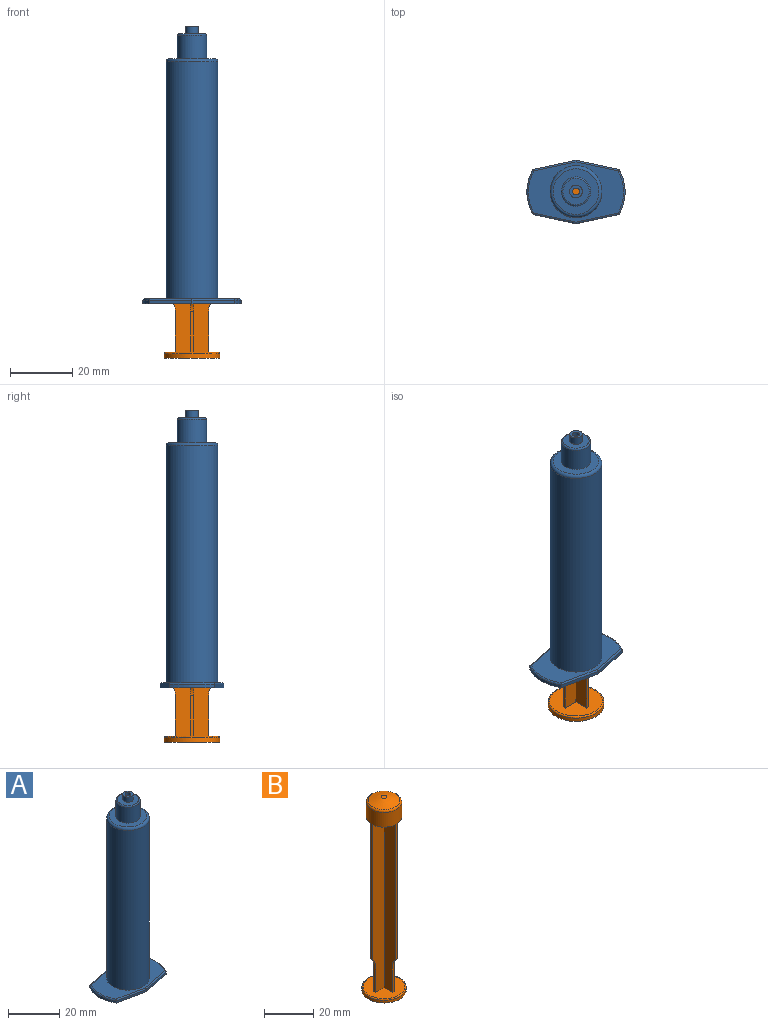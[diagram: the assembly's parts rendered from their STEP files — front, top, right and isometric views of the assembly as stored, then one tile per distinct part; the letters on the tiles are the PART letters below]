
ASSEMBLY  parts=2 mates=1
PART A: 25 faces, bbox 33.8x20.3x89 mm
  f0: cylinder r=7.15mm len=77mm, axis (0,0,-1), area 3459.2mm2, adj f8,f12
  f1: cylinder r=14.22mm len=14.5mm, axis (0,0,-1), area 15.2mm2, adj f2,f6,f8,f19
  f2: plane 13.78x2.9mm, normal (-0.21,-0.98,0), area 14.1mm2, adj f1,f3,f8,f17
  f3: plane 13.78x2.9mm, normal (0.21,-0.98,0), area 14.1mm2, adj f2,f4,f8,f16
  f4: cylinder r=14.22mm len=14.5mm, axis (0,0,-1), area 15.2mm2, adj f3,f5,f8,f18
  f5: plane 13.75x2.9mm, normal (0.21,0.98,0), area 14.1mm2, adj f4,f6,f8,f20
  f6: plane 13.75x2.9mm, normal (-0.21,0.98,0), area 14.1mm2, adj f1,f5,f8,f21
  f7: plane 30.5x19.28mm, normal (0,0,1), area 259mm2, adj f9,f16,f17,f18,f19,f20,f21
  f8: plane 31.5x20.3mm, normal (0,0,-1), area 357.3mm2, adj f0,f1,f2,f3,f4,f5,f6
  f9: cylinder r=8.3mm len=76mm, axis (0,0,-1), area 3963.4mm2, adj f7,f15
  f10: plane 14.6x14.6mm, normal (0,0,1), area 98mm2, adj f13,f15
  f11: cylinder r=1.1mm len=12mm, axis (0,0,-1), area 82.9mm2, adj f12,f22
  f12: plane 14.3x14.3mm, normal (0,0,-1), area 156.8mm2, adj f0,f11
  f13: cylinder r=4.7mm len=9.4mm, axis (0,0,-1), area 221.5mm2, adj f10,f24
  f14: plane 8.4x8.4mm, normal (0,0,1), area 42.2mm2, adj f23,f24
  f15: torus R=7.3mm, axis (0,0,1), area 78.3mm2, adj f9,f10
  f16: cylinder r=0.5mm len=13.88mm, axis (-0.98,-0.21,0), area 11mm2, adj f3,f7,f17,f18
  f17: cylinder r=0.5mm len=13.88mm, axis (-0.98,0.21,0), area 11mm2, adj f2,f7,f16,f19
  f18: torus R=13.72mm, axis (0,0,1), area 11.7mm2, adj f4,f7,f16,f20
  f19: torus R=13.72mm, axis (0,0,1), area 11.7mm2, adj f1,f7,f17,f21
  f20: cylinder r=0.5mm len=13.85mm, axis (0.98,-0.21,0), area 10.9mm2, adj f5,f7,f18,f21
  f21: cylinder r=0.5mm len=13.85mm, axis (0.98,0.21,0), area 10.9mm2, adj f6,f7,f19,f20
  f22: plane 4.1x4.1mm, normal (0,0,1), area 9.4mm2, adj f11,f23
  f23: cylinder r=2.05mm len=4.1mm, axis (0,0,-1), area 32.2mm2, adj f14,f22
  f24: torus R=4.2mm, axis (0,0,1), area 22.3mm2, adj f13,f14
PART B: 28 faces, bbox 19.4x19.4x95.8 mm
  f0: plane 6.63x6.63mm, normal (0,0,-1), area 33.3mm2, adj f3,f14,f15
  f1: plane 6.63x6.63mm, normal (0,0,-1), area 33.3mm2, adj f3,f12,f13
  f2: plane 6.63x6.63mm, normal (0,0,-1), area 33.3mm2, adj f3,f10,f11
  f3: cylinder r=7.15mm len=74.28mm, axis (0,0,-1), area 595.2mm2, adj f0,f1,f2,f5,f7,f8,f9,f10
  f4: plane 2.3x2.3mm, normal (0,0,1), area 4.2mm2, adj f6
  f5: plane 6.63x6.63mm, normal (0,0,-1), area 33.3mm2, adj f3,f8,f9
  f6: cone r=1.15mm half-angle=71.6deg, axis (0,0,-1), area 134.1mm2, adj f4,f7
  f7: torus R=6.15mm, axis (0,0,1), area 54.2mm2, adj f3,f6
  f8: plane 84.04x6.68mm, normal (0,1,0), area 528.1mm2, adj f3,f5,f9,f16,f23,f26
  f9: plane 84.04x6.67mm, normal (-1,0,0), area 528.1mm2, adj f3,f5,f8,f17,f22,f26
  f10: plane 84.04x6.68mm, normal (1,0,0), area 528.1mm2, adj f2,f3,f11,f17,f22,f26
  f11: plane 84.04x6.67mm, normal (0,1,0), area 528.1mm2, adj f2,f3,f10,f18,f21,f26
  f12: plane 84.04x6.68mm, normal (0,-1,0), area 528.1mm2, adj f1,f3,f13,f18,f21,f26
  f13: plane 84.04x6.67mm, normal (1,0,0), area 528.1mm2, adj f1,f3,f12,f19,f20,f26
  f14: plane 84.04x6.68mm, normal (-1,0,0), area 528.1mm2, adj f0,f3,f15,f19,f20,f26
  f15: plane 84.04x6.67mm, normal (0,-1,0), area 528.1mm2, adj f0,f3,f14,f16,f23,f26
  f16: plane 13.13x1mm, normal (-1,0,0), area 13.1mm2, adj f8,f15,f23,f26
  f17: plane 13.13x1mm, normal (0,1,0), area 13.1mm2, adj f9,f10,f22,f26
  f18: plane 13.13x1mm, normal (1,0,0), area 13.1mm2, adj f11,f12,f21,f26
  f19: plane 13.13x1mm, normal (0,-1,0), area 13.1mm2, adj f13,f14,f20,f26
  f20: bspline ~3.88x1.85mm, area 4.5mm2, adj f3,f13,f14,f19
  f21: bspline ~3.88x1.85mm, area 4.5mm2, adj f3,f11,f12,f18
  f22: bspline ~3.88x1.85mm, area 4.5mm2, adj f3,f9,f10,f17
  f23: bspline ~3.88x1.85mm, area 4.5mm2, adj f3,f8,f15,f16
  f24: cylinder r=8.95mm len=17.9mm, axis (0,0,1), area 73.1mm2, adj f25,f27
  f25: plane 17.9x17.9mm, normal (0,0,-1), area 251.6mm2, adj f24
  f26: plane 16.9x16.9mm, normal (0,0,1), area 204.1mm2, adj f8,f9,f10,f11,f12,f13,f14,f15
  f27: torus R=8.45mm, axis (0,0,-1), area 43.3mm2, adj f24,f26
PLACE A at identity fixed
PLACE B t=(0,0,68.36)mm
MATE slider B.f3 <-> A.f0  axis (0,0,-1) through (0,0,38.5)mm
